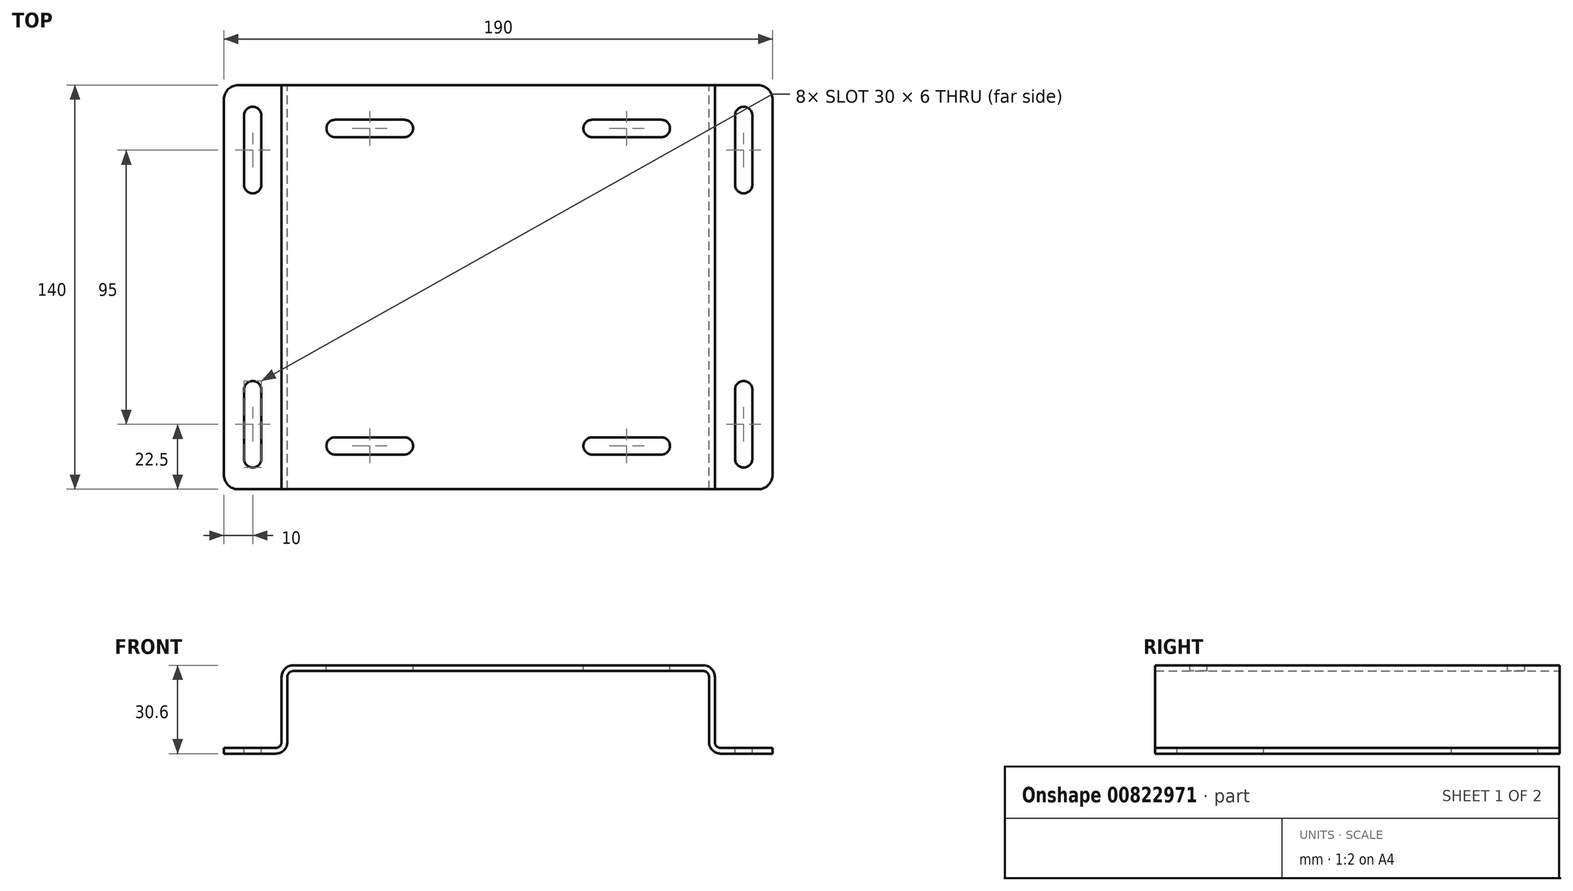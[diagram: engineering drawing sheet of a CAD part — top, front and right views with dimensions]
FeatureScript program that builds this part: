
annotation { "Feature Type Name" : "Feature", "Feature Type Description" : "" }
export const myFeature = defineFeature(function(context is Context, id is Id, definition is map)
    precondition{}
    {
        {
            var Q0;
            Q0=qCreatedBy(makeId("Front.planeOp"),FACE);
            var sketch = newSketch(context, id + "F0", { "sketchPlane" : qUnion([Q0])});
            skLineSegment(sketch, "E0.bottom", {"start": v(-75, -15.3) * mm, "end": v(75, -15.3) * mm, "construction": true});
            skLineSegment(sketch, "E0.top", {"start": v(-75, 15.3) * mm, "end": v(75, 15.3) * mm});
            skLineSegment(sketch, "E0.left", {"start": v(-75, -13.3) * mm, "end": v(-75, 15.3) * mm});
            skLineSegment(sketch, "E0.right", {"start": v(75, -13.3) * mm, "end": v(75, 15.3) * mm});
            skPoint(sketch, "E0.middle", {"position": v(0, 0) * mm});
            skLineSegment(sketch, "E1", {"start": v(0, 0) * mm, "end": v(0, -62.9) * mm, "construction": true});
            skLineSegment(sketch, "E2", {"start": v(-75, -15.3) * mm, "end": v(-95, -15.3) * mm});
            skLineSegment(sketch, "E3.MirrorCS", {"start": v(75, -15.3) * mm, "end": v(95, -15.3) * mm});
            skLineSegment(sketch, "E4", {"start": v(-95, -15.3) * mm, "end": v(-95, -13.3) * mm});
            skLineSegment(sketch, "E5", {"start": v(-95, -13.3) * mm, "end": v(-75, -13.3) * mm});
            skLineSegment(sketch, "E6", {"start": v(-73, -13.3) * mm, "end": v(-73, 13.3) * mm});
            skLineSegment(sketch, "E7", {"start": v(-73, 13.3) * mm, "end": v(73, 13.3) * mm});
            skLineSegment(sketch, "E8", {"start": v(73, 13.3) * mm, "end": v(73, -13.3) * mm});
            skLineSegment(sketch, "E9", {"start": v(75, -13.3) * mm, "end": v(95, -13.3) * mm});
            skLineSegment(sketch, "E10", {"start": v(95, -13.3) * mm, "end": v(95, -15.3) * mm});
            skLineSegment(sketch, "E11", {"start": v(73, -13.3) * mm, "end": v(73, -15.3) * mm});
            skLineSegment(sketch, "E12", {"start": v(73, -15.3) * mm, "end": v(75, -15.3) * mm});
            skLineSegment(sketch, "E13", {"start": v(-75, -15.3) * mm, "end": v(-73, -15.3) * mm});
            skLineSegment(sketch, "E14", {"start": v(-73, -15.3) * mm, "end": v(-73, -13.3) * mm});
            skSolve(sketch);
        }
        {
            var Q0;
            Q0 = qSketchRegion(id + "F0", true);
            extrude(context, id + "F1", {"entities" : qUnion([Q0]), "endBound" : BoundingType.SYMMETRIC, "depth" : 140 * mm, "offsetDistance" : 25 * mm});
        }
        {
            var Q0;
            Q0=makeQuery(id+"F1.opExtrude","SWEPT_EDGE",EDGE,{"disambiguationData":[OSD([sQuery(id+"F0.wireOp",EDGE,"E6"),sQuery(id+"F0.wireOp",EDGE,"E7")])]});
            var Q1;
            Q1=makeQuery(id+"F1.opExtrude","SWEPT_EDGE",EDGE,{"disambiguationData":[OSD([sQuery(id+"F0.wireOp",EDGE,"E7"),sQuery(id+"F0.wireOp",EDGE,"E8")])]});
            var Q2;
            Q2=makeQuery(id+"F1.opExtrude","SWEPT_EDGE",EDGE,{"disambiguationData":[OSD([sQuery(id+"F0.wireOp",EDGE,"E0.right"),sQuery(id+"F0.wireOp",EDGE,"E9")])]});
            var Q3;
            Q3=makeQuery(id+"F1.opExtrude","SWEPT_EDGE",EDGE,{"disambiguationData":[OSD([sQuery(id+"F0.wireOp",EDGE,"E0.left"),sQuery(id+"F0.wireOp",EDGE,"E5")])]});
            fillet(context, id + "F2", {"entities" : qUnion([Q0, Q1, Q2, Q3]), "radius" : 2 * mm, "tangentPropagation" : true, "allowEdgeOverflow" : false});
        }
        {
            var Q0;
            Q0=makeQuery(id+"F1.opExtrude","SWEPT_EDGE",EDGE,{"disambiguationData":[OSD([sQuery(id+"F0.wireOp",EDGE,"E0.top"),sQuery(id+"F0.wireOp",EDGE,"E0.left")])]});
            var Q1;
            Q1=makeQuery(id+"F1.opExtrude","SWEPT_EDGE",EDGE,{"disambiguationData":[OSD([sQuery(id+"F0.wireOp",EDGE,"E13"),sQuery(id+"F0.wireOp",EDGE,"E14")])]});
            var Q2;
            Q2=makeQuery(id+"F1.opExtrude","SWEPT_EDGE",EDGE,{"disambiguationData":[OSD([sQuery(id+"F0.wireOp",EDGE,"E11"),sQuery(id+"F0.wireOp",EDGE,"E12")])]});
            var Q3;
            Q3=makeQuery(id+"F1.opExtrude","SWEPT_EDGE",EDGE,{"disambiguationData":[OSD([sQuery(id+"F0.wireOp",EDGE,"E0.top"),sQuery(id+"F0.wireOp",EDGE,"E0.right")])]});
            fillet(context, id + "F3", {"entities" : qUnion([Q0, Q1, Q2, Q3]), "radius" : 4 * mm, "tangentPropagation" : true, "allowEdgeOverflow" : false});
        }
        {
            var Q0;
            Q0=makeQuery(id+"F1.opExtrude","SWEPT_FACE",FACE,{"disambiguationData":[OSD([sQuery(id+"F0.wireOp",EDGE,"E9")])]});
            var sketch = newSketch(context, id + "F4", { "sketchPlane" : qUnion([Q0])});
            skLineSegment(sketch, "E15.0", {"start": v(-95, -70) * mm, "end": v(-95, 70) * mm, "construction": true});
            skLineSegment(sketch, "E16.0", {"start": v(95, -70) * mm, "end": v(95, 70) * mm, "construction": true});
            skLineSegment(sketch, "E17", {"start": v(0, 0) * mm, "end": v(-85, 0) * mm, "construction": true});
            skLineSegment(sketch, "E18", {"start": v(-85, 0) * mm, "end": v(-85, 62.5) * mm, "construction": true});
            skArc(sketch, "E19", {"start": v(-82, 59.5) * mm, "mid": v(-85, 62.5) * mm, "end": v(-88, 59.5) * mm});
            skArc(sketch, "E20", {"start": v(-88, 35.5) * mm, "mid": v(-85, 32.5) * mm, "end": v(-82, 35.5) * mm});
            skLineSegment(sketch, "E21", {"start": v(-85, 59.5) * mm, "end": v(-88, 59.5) * mm, "construction": true});
            skLineSegment(sketch, "E22", {"start": v(-88, 59.5) * mm, "end": v(-88, 35.5) * mm});
            skLineSegment(sketch, "E23", {"start": v(-88, 35.5) * mm, "end": v(-85, 35.5) * mm, "construction": true});
            skLineSegment(sketch, "E24.MirrorCS", {"start": v(-82, 59.5) * mm, "end": v(-82, 35.5) * mm});
            skLineSegment(sketch, "E25.MirrorCS", {"start": v(-88, -59.5) * mm, "end": v(-88, -35.5) * mm});
            skArc(sketch, "E26.MirrorCS", {"start": v(-88, -35.5) * mm, "mid": v(-85, -32.5) * mm, "end": v(-82, -35.5) * mm});
            skArc(sketch, "E27.MirrorCS", {"start": v(-82, -59.5) * mm, "mid": v(-85, -62.5) * mm, "end": v(-88, -59.5) * mm});
            skLineSegment(sketch, "E28.MirrorCS", {"start": v(-82, -59.5) * mm, "end": v(-82, -35.5) * mm});
            skLineSegment(sketch, "E29", {"start": v(0, 0) * mm, "end": v(0, 73.27) * mm, "construction": true});
            skArc(sketch, "E30.MirrorCS", {"start": v(82, -59.5) * mm, "mid": v(85, -62.5) * mm, "end": v(88, -59.5) * mm});
            skArc(sketch, "E31.MirrorCS", {"start": v(88, -35.5) * mm, "mid": v(85, -32.5) * mm, "end": v(82, -35.5) * mm});
            skLineSegment(sketch, "E32.MirrorCS", {"start": v(88, -59.5) * mm, "end": v(88, -35.5) * mm});
            skLineSegment(sketch, "E33.MirrorCS", {"start": v(82, -59.5) * mm, "end": v(82, -35.5) * mm});
            skLineSegment(sketch, "E34.MirrorCS", {"start": v(82, 59.5) * mm, "end": v(82, 35.5) * mm});
            skArc(sketch, "E35.MirrorCS", {"start": v(88, 35.5) * mm, "mid": v(85, 32.5) * mm, "end": v(82, 35.5) * mm});
            skLineSegment(sketch, "E36.MirrorCS", {"start": v(88, 59.5) * mm, "end": v(88, 35.5) * mm});
            skArc(sketch, "E37.MirrorCS", {"start": v(82, 59.5) * mm, "mid": v(85, 62.5) * mm, "end": v(88, 59.5) * mm});
            skSolve(sketch);
        }
        {
            var Q0;
            Q0 = qSketchRegion(id + "F4", true);
            extrude(context, id + "F5", {"entities" : qUnion([Q0]), "operationType" : NewBodyOperationType.REMOVE, "oppositeDirection" : true, "depth" : 25 * mm, "offsetDistance" : 25 * mm});
        }
        {
            var Q0;
            Q0=makeQuery(id+"F1.opExtrude","CAP_EDGE",EDGE,{"disambiguationData":[OSD([sQuery(id+"F0.wireOp",EDGE,"E4")])],"isStart":true});
            var Q1;
            Q1=makeQuery(id+"F1.opExtrude","CAP_EDGE",EDGE,{"disambiguationData":[OSD([sQuery(id+"F0.wireOp",EDGE,"E10")])],"isStart":true});
            var Q2;
            Q2=makeQuery(id+"F1.opExtrude","CAP_EDGE",EDGE,{"disambiguationData":[OSD([sQuery(id+"F0.wireOp",EDGE,"E4")])],"isStart":false});
            var Q3;
            Q3=makeQuery(id+"F1.opExtrude","CAP_EDGE",EDGE,{"disambiguationData":[OSD([sQuery(id+"F0.wireOp",EDGE,"E10")])],"isStart":false});
            fillet(context, id + "F6", {"entities" : qUnion([Q0, Q1, Q2, Q3]), "radius" : 5 * mm, "tangentPropagation" : true, "allowEdgeOverflow" : false});
        }
        {
            var Q0;
            Q0=makeQuery(id+"F1.opExtrude","SWEPT_FACE",FACE,{"disambiguationData":[OSD([sQuery(id+"F0.wireOp",EDGE,"E0.top")])]});
            var sketch = newSketch(context, id + "F7", { "sketchPlane" : qUnion([Q0])});
            skLineSegment(sketch, "E38.bottom", {"start": v(44.5, 55) * mm, "end": v(-44.5, 55) * mm, "construction": true});
            skLineSegment(sketch, "E38.top", {"start": v(44.5, -55) * mm, "end": v(-44.5, -55) * mm, "construction": true});
            skLineSegment(sketch, "E38.left", {"start": v(44.5, 55) * mm, "end": v(44.5, -55) * mm, "construction": true});
            skLineSegment(sketch, "E38.right", {"start": v(-44.5, 55) * mm, "end": v(-44.5, -55) * mm, "construction": true});
            skPoint(sketch, "E38.middle", {"position": v(0, 0) * mm});
            skLineSegment(sketch, "E39", {"start": v(0, 0) * mm, "end": v(110.79, 0) * mm, "construction": true});
            skLineSegment(sketch, "E40", {"start": v(0, 0) * mm, "end": v(0, 74.36) * mm, "construction": true});
            skArc(sketch, "E41", {"start": v(-32.5, 52) * mm, "mid": v(-29.5, 55) * mm, "end": v(-32.5, 58) * mm});
            skLineSegment(sketch, "E42", {"start": v(-32.5, 55) * mm, "end": v(-32.5, 58) * mm, "construction": true});
            skLineSegment(sketch, "E43", {"start": v(-32.5, 58) * mm, "end": v(-56.5, 58) * mm});
            skLineSegment(sketch, "E44", {"start": v(-56.5, 58) * mm, "end": v(-56.5, 55) * mm, "construction": true});
            skArc(sketch, "E45", {"start": v(-56.5, 58) * mm, "mid": v(-59.5, 55) * mm, "end": v(-56.5, 52) * mm});
            skLineSegment(sketch, "E46.MirrorCS", {"start": v(-32.5, 52) * mm, "end": v(-56.5, 52) * mm});
            skArc(sketch, "E47.MirrorCS", {"start": v(32.5, 52) * mm, "mid": v(29.5, 55) * mm, "end": v(32.5, 58) * mm});
            skLineSegment(sketch, "E48.MirrorCS", {"start": v(32.5, 58) * mm, "end": v(56.5, 58) * mm});
            skLineSegment(sketch, "E49.MirrorCS", {"start": v(32.5, 52) * mm, "end": v(56.5, 52) * mm});
            skArc(sketch, "E50.MirrorCS", {"start": v(56.5, 58) * mm, "mid": v(59.5, 55) * mm, "end": v(56.5, 52) * mm});
            skArc(sketch, "E51.MirrorCS", {"start": v(56.5, -58) * mm, "mid": v(59.5, -55) * mm, "end": v(56.5, -52) * mm});
            skArc(sketch, "E52.MirrorCS", {"start": v(32.5, -52) * mm, "mid": v(29.5, -55) * mm, "end": v(32.5, -58) * mm});
            skLineSegment(sketch, "E53.MirrorCS", {"start": v(32.5, -58) * mm, "end": v(56.5, -58) * mm});
            skLineSegment(sketch, "E54.MirrorCS", {"start": v(32.5, -52) * mm, "end": v(56.5, -52) * mm});
            skArc(sketch, "E55.MirrorCS", {"start": v(-32.5, -52) * mm, "mid": v(-29.5, -55) * mm, "end": v(-32.5, -58) * mm});
            skLineSegment(sketch, "E56.MirrorCS", {"start": v(-32.5, -52) * mm, "end": v(-56.5, -52) * mm});
            skLineSegment(sketch, "E57.MirrorCS", {"start": v(-32.5, -58) * mm, "end": v(-56.5, -58) * mm});
            skArc(sketch, "E58.MirrorCS", {"start": v(-56.5, -58) * mm, "mid": v(-59.5, -55) * mm, "end": v(-56.5, -52) * mm});
            skSolve(sketch);
        }
        {
            var Q0;
            Q0 = qSketchRegion(id + "F7", true);
            extrude(context, id + "F8", {"entities" : qUnion([Q0]), "operationType" : NewBodyOperationType.REMOVE, "oppositeDirection" : true, "depth" : 25 * mm, "offsetDistance" : 25 * mm});
        }
    });
